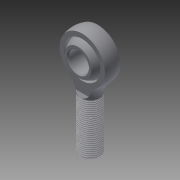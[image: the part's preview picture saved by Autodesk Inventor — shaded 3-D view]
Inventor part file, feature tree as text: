
AUTODESK INVENTOR PART (.ipt)
format: ipt  version: 2015 (Build 190159000, 159)  size: 1,169,408 bytes
history: native  units: in
note: dims shown in document units (in); Inventor stores cm internally (conversion verified against a paired STEP export)
features: other x2, imported_body x2, chamfer x1
ambient origin geometry x8: Origin, YZ Plane, XZ Plane, XY Plane, X Axis, Y Axis, Z Axis, Center Point
bodies: Body1 (feature_tree), Body2 (feature_tree)
feature tree (5):
  other  "Cut-Extrude2"
  other  "BallJoint1"
  chamfer  "Chamfer1"  [1 undecoded]
  imported_body  "Base1"
  imported_body  "Base2"
note: 1 required parameter value undecoded (feature->parameter linkage not recoverable at this tier; creation-order binding heuristic only, values carry confidence <= 0.55)
